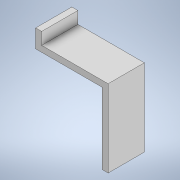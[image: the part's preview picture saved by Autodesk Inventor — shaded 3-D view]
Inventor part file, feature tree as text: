
AUTODESK INVENTOR PART (.ipt)
format: ipt  version: 2022 (Build 260153000, 153)  size: 114,688 bytes
history: native  units: mm
features: extrude x3, sketch x3
ambient origin geometry x8: Origin, YZ Plane, XZ Plane, XY Plane, X Axis, Y Axis, Z Axis, Center Point
bodies: Solid1 (feature_tree)
feature tree (6):
  extrude  "Extrusion1"  Depth=30.0mm
  extrude  "Extrusion2"  Depth=5.0mm
  extrude  "Extrusion3"  Depth=5.0mm
  sketch  "Sketch1"  dims[d0=60.0mm d1=30.0mm]
  sketch  "Sketch2"  dims[d2=5.0mm d3=0.0mm d4=5.0mm]
  sketch  "Sketch3"  dims[d5=10.0mm d6=0.0mm d7=5.0mm d8=59.0mm d9=0.0mm]
